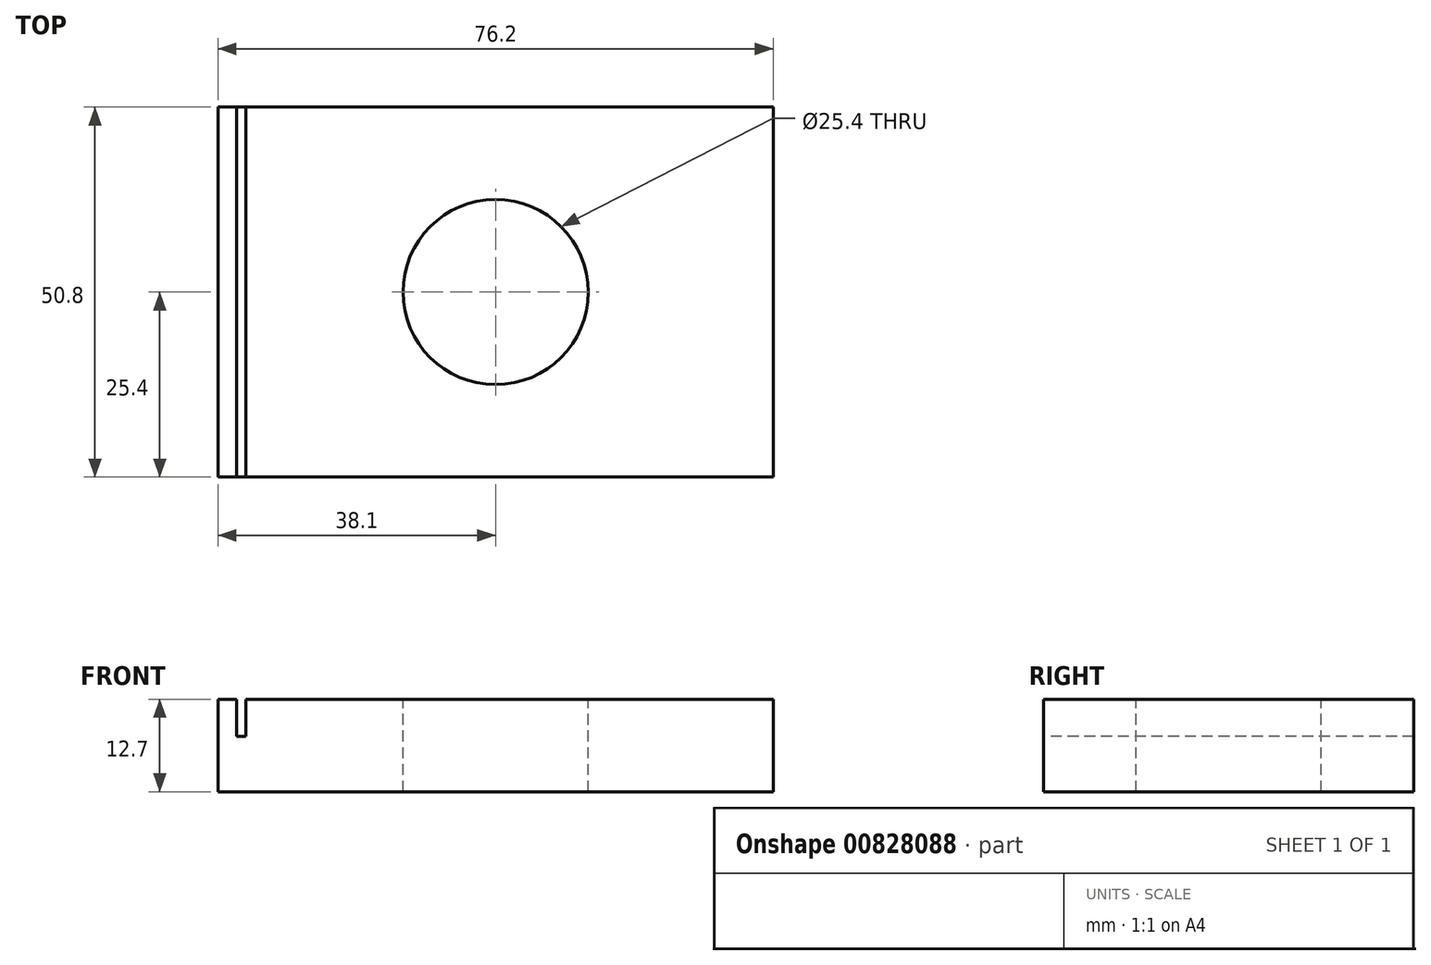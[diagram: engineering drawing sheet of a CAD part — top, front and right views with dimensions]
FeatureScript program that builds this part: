
annotation { "Feature Type Name" : "Feature", "Feature Type Description" : "" }
export const myFeature = defineFeature(function(context is Context, id is Id, definition is map)
    precondition{}
    {
        {
            var Q0;
            Q0=qCreatedBy(makeId("Top.planeOp"),FACE);
            var sketch = newSketch(context, id + "F0", { "sketchPlane" : qUnion([Q0])});
            skLineSegment(sketch, "E0.bottom", {"start": v(-38.1, 25.4) * mm, "end": v(38.1, 25.4) * mm});
            skLineSegment(sketch, "E0.top", {"start": v(-38.1, -25.4) * mm, "end": v(38.1, -25.4) * mm});
            skLineSegment(sketch, "E0.left", {"start": v(-38.1, 25.4) * mm, "end": v(-38.1, -25.4) * mm});
            skLineSegment(sketch, "E0.right", {"start": v(38.1, 25.4) * mm, "end": v(38.1, -25.4) * mm});
            skPoint(sketch, "E0.middle", {"position": v(0, 0) * mm});
            skSolve(sketch);
        }
        {
            var Q0;
            Q0 = qSketchRegion(id + "F0", true);
            var Q1;
            Q1=makeQuery(id+"F0.imprint","IMPRINT",FACE,{"disambiguationData":[TD([[makeQuery(id+"F0.imprint","IMPRINT",EDGE,{"derivedFrom":sQuery(id+"F0.wireOp",EDGE,"E0.bottom")}),-1.0]])]});
            extrude(context, id + "F1", {"entities" : qUnion([Q0, Q1]), "depth" : 12.7 * mm, "offsetDistance" : 25.4 * mm});
        }
        {
            var Q0;
            Q0=makeQuery(id+"F1.opExtrude","CAP_FACE",FACE,{"disambiguationData":[OSD([sQuery(id+"F0.wireOp",EDGE,"E0.bottom"),sQuery(id+"F0.wireOp",EDGE,"E0.top"),sQuery(id+"F0.wireOp",EDGE,"E0.left"),sQuery(id+"F0.wireOp",EDGE,"E0.right")])],"isStart":false});
            var sketch = newSketch(context, id + "F2", { "sketchPlane" : qUnion([Q0])});
            skCircle(sketch, "E1", {"center": v(0, 0) * mm, "radius": 12.7 * mm});
            skSolve(sketch);
        }
        {
            var Q0;
            Q0=makeQuery(id+"F2.imprint","IMPRINT",FACE,{"disambiguationData":[TD([[makeQuery(id+"F2.imprint","IMPRINT",EDGE,{"derivedFrom":sQuery(id+"F2.wireOp",EDGE,"E1")}),1.0]])]});
            extrude(context, id + "F3", {"entities" : qUnion([Q0]), "operationType" : NewBodyOperationType.REMOVE, "oppositeDirection" : true, "depth" : 25.4 * mm, "offsetDistance" : 25.4 * mm});
        }
        {
            var Q0;
            Q0=makeQuery(id+"F1.opExtrude","SWEPT_FACE",FACE,{"disambiguationData":[OSD([sQuery(id+"F0.wireOp",EDGE,"E0.top")])]});
            var sketch = newSketch(context, id + "F4", { "sketchPlane" : qUnion([Q0])});
            skLineSegment(sketch, "E2.bottom", {"start": v(-35.56, 12.7) * mm, "end": v(-34.28, 12.7) * mm});
            skLineSegment(sketch, "E2.top", {"start": v(-35.56, 12.36) * mm, "end": v(-34.28, 12.36) * mm});
            skLineSegment(sketch, "E2.left", {"start": v(-35.56, 12.7) * mm, "end": v(-35.56, 12.36) * mm});
            skLineSegment(sketch, "E2.right", {"start": v(-34.28, 12.7) * mm, "end": v(-34.28, 12.36) * mm});
            skLineSegment(sketch, "E3.left", {"start": v(-35.56, 12.7) * mm, "end": v(-35.56, 12.7) * mm});
            skLineSegment(sketch, "E3.right", {"start": v(-34.28, 12.7) * mm, "end": v(-34.28, 12.7) * mm});
            skLineSegment(sketch, "E4.top", {"start": v(-35.56, 7.61) * mm, "end": v(-34.28, 7.61) * mm});
            skLineSegment(sketch, "E4.left", {"start": v(-35.56, 12.7) * mm, "end": v(-35.56, 7.61) * mm});
            skLineSegment(sketch, "E4.right", {"start": v(-34.28, 12.7) * mm, "end": v(-34.28, 7.61) * mm});
            skSolve(sketch);
        }
        {
            var Q0;
            {var subQ0=sQuery(id+"F4.wireOp",EDGE,"E2.top");Q0=makeQuery(id+"F4.imprint","IMPRINT",FACE,{"disambiguationData":[TD([[makeQuery(id+"F4.imprint","IMPRINT",EDGE,{"derivedFrom":subQ0}),1.0]])]});}
            var Q1;
            {var subQ0=sQuery(id+"F4.wireOp",EDGE,"E2.top");Q1=makeQuery(id+"F4.imprint","IMPRINT",FACE,{"disambiguationData":[TD([[makeQuery(id+"F4.imprint","IMPRINT",EDGE,{"derivedFrom":subQ0}),-1.0]])]});}
            extrude(context, id + "F5", {"entities" : qUnion([Q0, Q1]), "operationType" : NewBodyOperationType.REMOVE, "oppositeDirection" : true, "depth" : 50.85 * mm, "offsetDistance" : 25.4 * mm});
        }
    });
